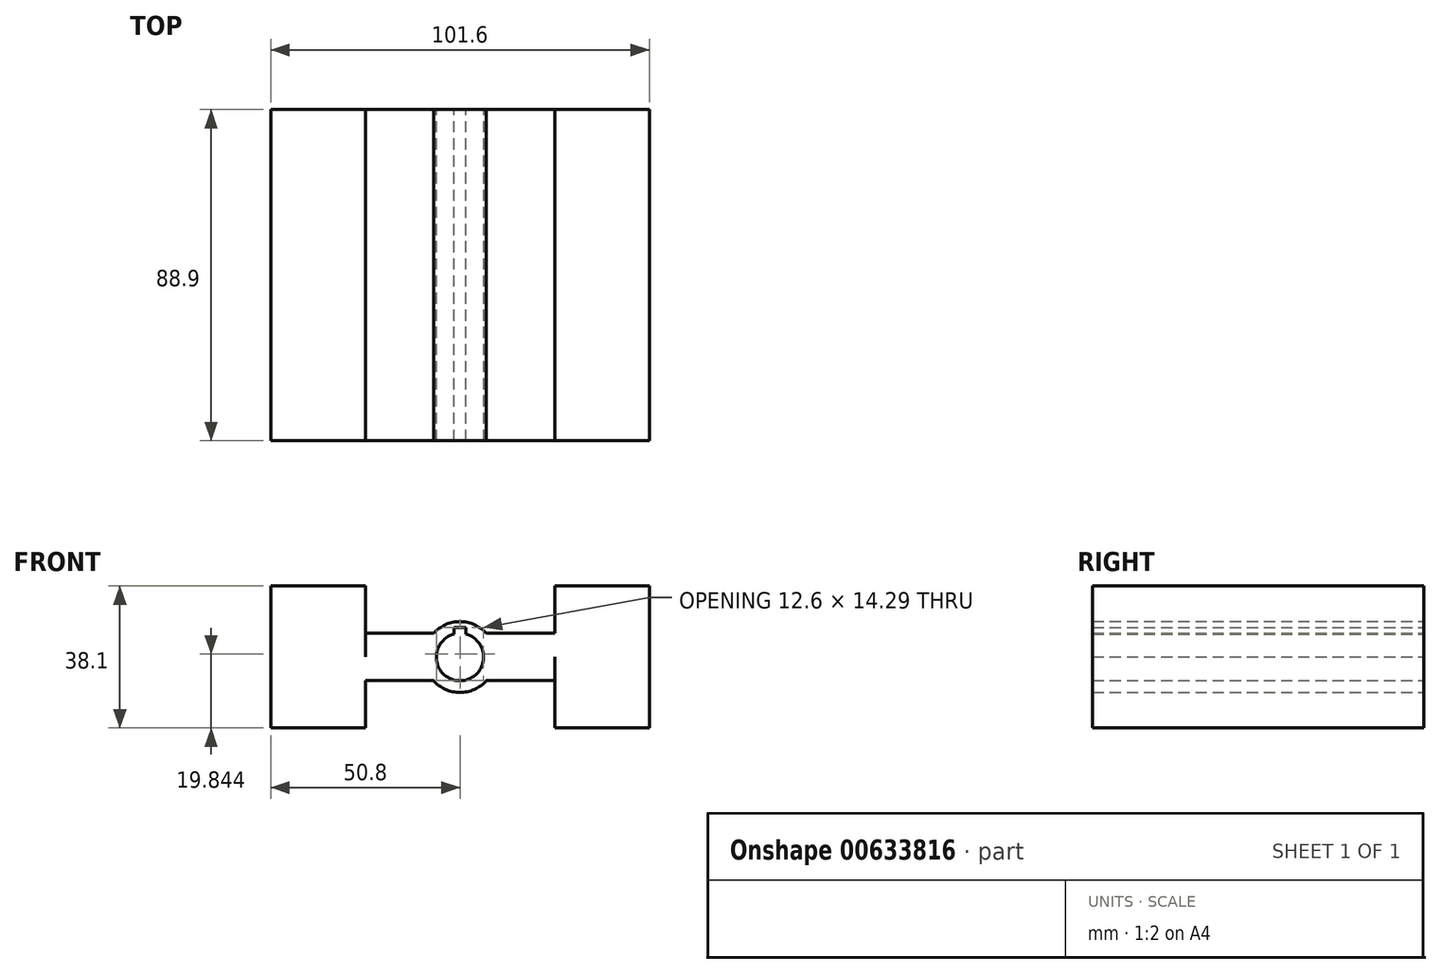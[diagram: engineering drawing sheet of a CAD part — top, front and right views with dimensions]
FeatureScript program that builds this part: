
annotation { "Feature Type Name" : "Feature", "Feature Type Description" : "" }
export const myFeature = defineFeature(function(context is Context, id is Id, definition is map)
    precondition{}
    {
        {
            var Q0;
            Q0=qCreatedBy(makeId("Front.planeOp"),FACE);
            var sketch = newSketch(context, id + "F0", { "sketchPlane" : qUnion([Q0]), "disableImprinting" : false});
            skLineSegment(sketch, "E0.left", {"start": v(-25.4, 6.35) * mm, "end": v(-25.4, -6.35) * mm});
            skLineSegment(sketch, "E0.right", {"start": v(25.4, 6.35) * mm, "end": v(25.4, -6.35) * mm});
            skPoint(sketch, "E0.middle", {"position": v(0, 0) * mm});
            skCircle(sketch, "E1", {"center": v(0, 0) * mm, "radius": 6.35 * mm});
            skLineSegment(sketch, "E2", {"start": v(-1.59, 7.94) * mm, "end": v(1.59, 7.94) * mm});
            skLineSegment(sketch, "E3", {"start": v(1.59, 7.94) * mm, "end": v(1.59, 4.76) * mm});
            skLineSegment(sketch, "E4", {"start": v(1.59, 4.76) * mm, "end": v(-1.59, 4.76) * mm});
            skLineSegment(sketch, "E5", {"start": v(-1.59, 4.76) * mm, "end": v(-1.59, 7.94) * mm});
            skLineSegment(sketch, "E6.bottom", {"start": v(-25.4, 19.05) * mm, "end": v(-50.8, 19.05) * mm});
            skLineSegment(sketch, "E6.top", {"start": v(-25.4, -19.05) * mm, "end": v(-50.8, -19.05) * mm});
            skLineSegment(sketch, "E6.left", {"start": v(-25.4, 19.05) * mm, "end": v(-25.4, -19.05) * mm});
            skLineSegment(sketch, "E6.right", {"start": v(-50.8, 19.05) * mm, "end": v(-50.8, -19.05) * mm});
            skPoint(sketch, "E6.middle", {"position": v(-38.1, 0) * mm});
            skPoint(sketch, "E6.middle.positionSnap0", {"position": v(-25.4, 0) * mm});
            skPoint(sketch, "E6.cornerSnap0", {"position": v(-25.4, 0) * mm});
            skPoint(sketch, "E6.centerSnap0", {"position": v(-25.4, 0) * mm});
            skLineSegment(sketch, "E7.bottom", {"start": v(25.4, 19.05) * mm, "end": v(50.8, 19.05) * mm});
            skLineSegment(sketch, "E7.top", {"start": v(25.4, -19.05) * mm, "end": v(50.8, -19.05) * mm});
            skLineSegment(sketch, "E7.left", {"start": v(25.4, 19.05) * mm, "end": v(25.4, -19.05) * mm});
            skLineSegment(sketch, "E7.right", {"start": v(50.8, 19.05) * mm, "end": v(50.8, -19.05) * mm});
            skPoint(sketch, "E7.middle", {"position": v(38.1, 0) * mm});
            skPoint(sketch, "E7.cornerSnap0", {"position": v(25.4, 0) * mm});
            skCircle(sketch, "E8", {"center": v(0, 0) * mm, "radius": 9.53 * mm});
            skLineSegment(sketch, "E9", {"start": v(-25.4, 6.35) * mm, "end": v(-7.1, 6.35) * mm});
            skLineSegment(sketch, "E10", {"start": v(-25.4, -6.35) * mm, "end": v(-7.1, -6.35) * mm});
            skLineSegment(sketch, "E11", {"start": v(25.4, 6.35) * mm, "end": v(7.1, 6.35) * mm});
            skLineSegment(sketch, "E12", {"start": v(25.4, -6.35) * mm, "end": v(7.1, -6.35) * mm});
            skSolve(sketch);
        }
        {
            var Q0;
            Q0 = qSketchRegion(id + "F0", true);
            extrude(context, id + "F1", {"entities" : qUnion([Q0]), "domain" : OperationDomain.MODEL, "flatOperationType" : FlatOperationType.REMOVE, "depth" : 88.9 * mm, "offsetDistance" : 25.4 * mm});
        }
    });
